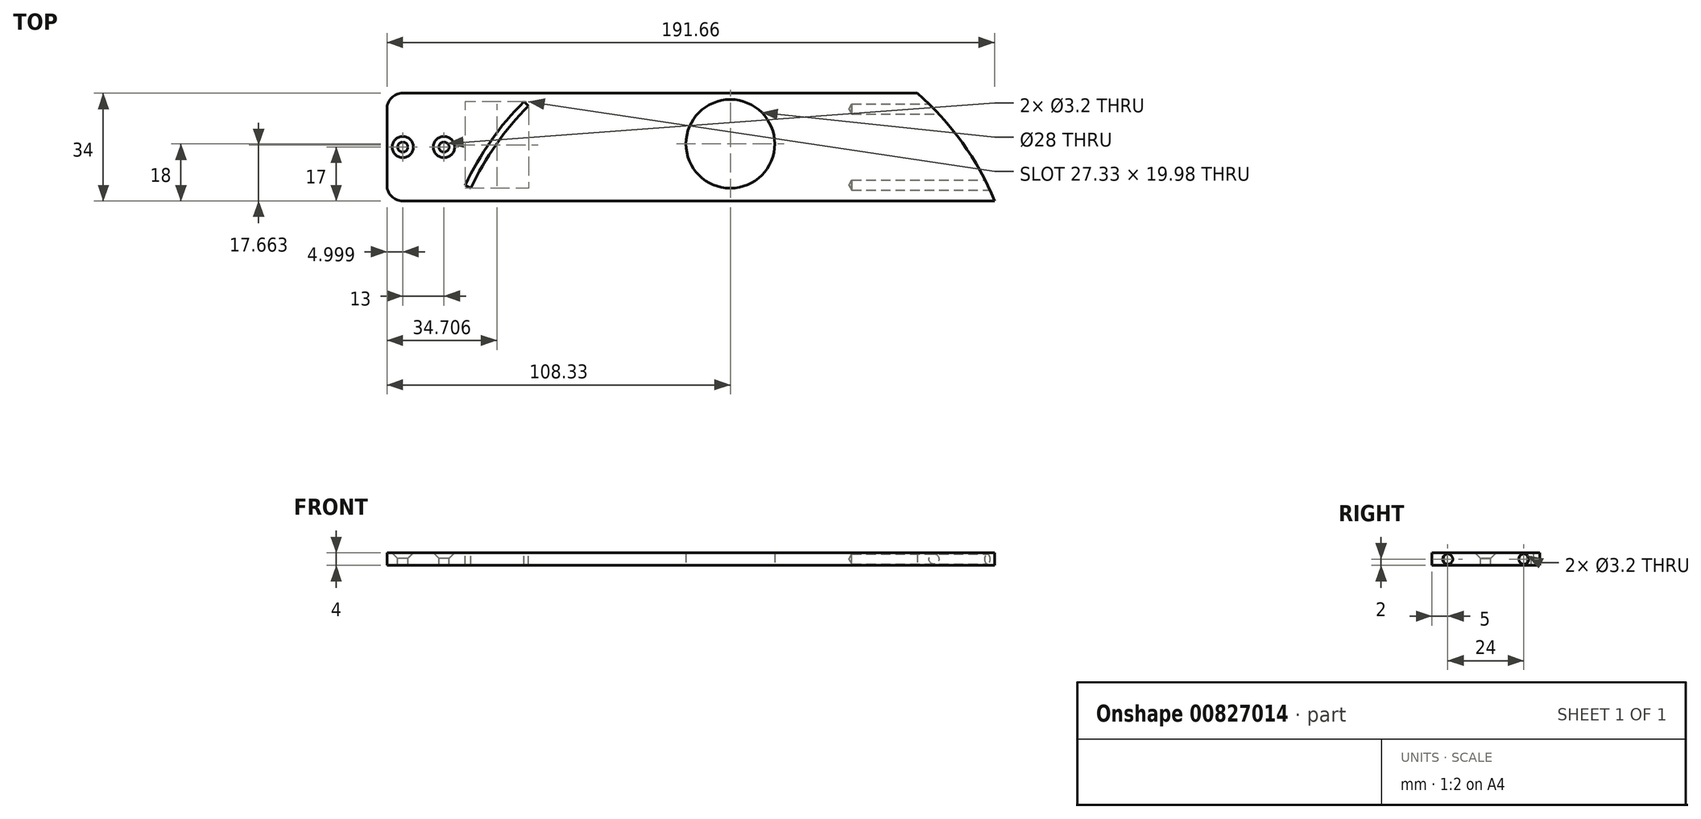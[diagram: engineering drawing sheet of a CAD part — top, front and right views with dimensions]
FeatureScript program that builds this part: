
annotation { "Feature Type Name" : "Feature", "Feature Type Description" : "" }
export const myFeature = defineFeature(function(context is Context, id is Id, definition is map)
    precondition{}
    {
        {
            var Q0;
            Q0=qCreatedBy(makeId("Top.planeOp"),FACE);
            var sketch = newSketch(context, id + "F0", { "sketchPlane" : qUnion([Q0])});
            skCircle(sketch, "E0", {"center": v(0, 0) * mm, "radius": 90 * mm, "construction": true});
            skLineSegment(sketch, "E1", {"start": v(-73.46, 52) * mm, "end": v(73.46, 52) * mm, "construction": true});
            skLineSegment(sketch, "E2", {"start": v(0, 0) * mm, "end": v(0, 90) * mm, "construction": true});
            skCircle(sketch, "E3", {"center": v(0, 52) * mm, "radius": 14 * mm, "construction": true});
            skLineSegment(sketch, "E4.0", {"start": v(-58.96, 68) * mm, "end": v(58.96, 68) * mm, "construction": true});
            skLineSegment(sketch, "E5.MirrorCS", {"start": v(-73.46, 84) * mm, "end": v(73.46, 84) * mm, "construction": true});
            skLineSegment(sketch, "E6.0", {"start": v(-83.33, 34) * mm, "end": v(83.33, 34) * mm, "construction": true});
            skArc(sketch, "E7", {"start": v(83.33, 34) * mm, "mid": v(73.15, 52.44) * mm, "end": v(58.96, 68) * mm});
            skLineSegment(sketch, "E8", {"start": v(-58.96, 68) * mm, "end": v(58.96, 68) * mm});
            skLineSegment(sketch, "E9", {"start": v(-58.96, 68) * mm, "end": v(-108.33, 68) * mm});
            skLineSegment(sketch, "E10", {"start": v(-83.33, 34) * mm, "end": v(-108.33, 34) * mm});
            skLineSegment(sketch, "E11", {"start": v(83.33, 34) * mm, "end": v(-83.33, 34) * mm});
            skLineSegment(sketch, "E12", {"start": v(-108.33, 34) * mm, "end": v(-108.33, 68) * mm});
            skCircle(sketch, "E13", {"center": v(0, 52) * mm, "radius": 57.5 * mm, "construction": true});
            skSolve(sketch);
        }
        {
            var Q0;
            Q0=qCreatedBy(makeId("Right.planeOp"),FACE);
            cPlane(context, id + "F1", {"entities" : qUnion([Q0]), "cplaneType" : CPlaneType.OFFSET, "offset" : 87.27 * mm, "width" : 150 * mm, "height" : 150 * mm});
        }
        {
            var Q0;
            Q0=qCreatedBy(id+"F1.planeOp",FACE);
            var sketch = newSketch(context, id + "F2", { "sketchPlane" : qUnion([Q0])});
            skSolve(sketch);
        }
        {
            var Q0;
            Q0=makeQuery(id+"F0.imprint","IMPRINT",FACE,{"disambiguationData":[TD([[makeQuery(id+"F0.imprint","IMPRINT",EDGE,{"derivedFrom":sQuery(id+"F0.wireOp",EDGE,"E7")}),1.0]])]});
            var Q1;
            Q1 = qSketchRegion(id + "F2", true);
            extrude(context, id + "F3", {"entities" : qUnion([Q0, Q1]), "depth" : 4 * mm, "offsetDistance" : 25 * mm});
        }
        {
            var Q0;
            Q0=makeQuery(id+"F0.imprint","IMPRINT",FACE,{"disambiguationData":[TD([[makeQuery(id+"F0.imprint","IMPRINT",EDGE,{"derivedFrom":sQuery(id+"F0.wireOp",EDGE,"E7")}),1.0]])]});
            extrude(context, id + "F4", {"entities" : qUnion([Q0]), "operationType" : NewBodyOperationType.ADD, "depth" : 4 * mm, "offsetDistance" : 25 * mm});
        }
        {
            var Q0;
            Q0=qCreatedBy(makeId("Right.planeOp"),FACE);
            cPlane(context, id + "F5", {"entities" : qUnion([Q0]), "cplaneType" : CPlaneType.OFFSET, "offset" : 83.3 * mm, "width" : 150 * mm, "height" : 150 * mm});
        }
        {
            var Q0;
            Q0=qCreatedBy(id+"F5.planeOp",FACE);
            var sketch = newSketch(context, id + "F6", { "sketchPlane" : qUnion([Q0])});
            skLineSegment(sketch, "E14", {"start": v(34.24, 2) * mm, "end": v(67.83, 2) * mm, "construction": true});
            skPoint(sketch, "E15", {"position": v(63, 2) * mm});
            skPoint(sketch, "E16", {"position": v(39, 2) * mm});
            skSolve(sketch);
        }
        {
            var Q0;
            Q0=sQuery(id+"F6.wireOp",VERTEX,"E15");
            var Q1;
            Q1=sQuery(id+"F6.wireOp",VERTEX,"E16");
            var Q2;
            Q2=makeQuery(id+"F3.opExtrude","SWEPT_BODY",BODY,{"disambiguationData":[OSD([sQuery(id+"F0.wireOp",EDGE,"E7"),sQuery(id+"F0.wireOp",EDGE,"E8"),sQuery(id+"F0.wireOp",EDGE,"E9"),sQuery(id+"F0.wireOp",EDGE,"E10"),sQuery(id+"F0.wireOp",EDGE,"E11"),sQuery(id+"F0.wireOp",EDGE,"E12")])]});
            hole(context, id + "F7", {"style" : HoleStyle.SIMPLE, "endStyle" : HoleEndStyle.BLIND, "holeDiameter" : 3.2 * mm, "majorDiameter" : 5 * mm, "holeDepth" : 45 * mm, "isTappedThrough" : true, "tappedDepth" : 12 * mm, "tapClearance" : 3, "startFromSketch" : true, "locations" : qUnion([Q0, Q1]), "scope" : qUnion([Q2])});
        }
        {
            var Q0;
            Q0=sQuery(id+"F0.wireOp",VERTEX,"E3.center");
            var Q1;
            Q1=makeQuery(id+"F3.opExtrude","SWEPT_BODY",BODY,{"disambiguationData":[OSD([sQuery(id+"F0.wireOp",EDGE,"E7"),sQuery(id+"F0.wireOp",EDGE,"E8"),sQuery(id+"F0.wireOp",EDGE,"E9"),sQuery(id+"F0.wireOp",EDGE,"E10"),sQuery(id+"F0.wireOp",EDGE,"E11"),sQuery(id+"F0.wireOp",EDGE,"E12")])]});
            hole(context, id + "F8", {"style" : HoleStyle.SIMPLE, "endStyle" : HoleEndStyle.THROUGH, "oppositeDirection" : true, "holeDiameter" : 28 * mm, "majorDiameter" : 5 * mm, "isTappedThrough" : true, "tappedDepth" : 12 * mm, "tapClearance" : 3, "startFromSketch" : true, "locations" : qUnion([Q0]), "scope" : qUnion([Q1])});
        }
        {
            var Q0;
            Q0=makeQuery(id+"F3.opExtrude","CAP_FACE",FACE,{"disambiguationData":[OSD([sQuery(id+"F0.wireOp",EDGE,"E7"),sQuery(id+"F0.wireOp",EDGE,"E8"),sQuery(id+"F0.wireOp",EDGE,"E9"),sQuery(id+"F0.wireOp",EDGE,"E10"),sQuery(id+"F0.wireOp",EDGE,"E11"),sQuery(id+"F0.wireOp",EDGE,"E12")])],"isStart":false});
            var sketch = newSketch(context, id + "F9", { "sketchPlane" : qUnion([Q0])});
            skLineSegment(sketch, "E17", {"start": v(-83.33, 34) * mm, "end": v(-83.33, 68) * mm, "construction": true});
            skLineSegment(sketch, "E18", {"start": v(-108.33, 51) * mm, "end": v(-83.33, 51) * mm, "construction": true});
            skPoint(sketch, "E19", {"position": v(-90.33, 51) * mm});
            skPoint(sketch, "E20", {"position": v(-103.33, 51) * mm});
            skSolve(sketch);
        }
        {
            var Q0;
            Q0=sQuery(id+"F9.wireOp",VERTEX,"E20");
            var Q1;
            Q1=sQuery(id+"F9.wireOp",VERTEX,"E19");
            var Q2;
            Q2=makeQuery(id+"F3.opExtrude","SWEPT_BODY",BODY,{"disambiguationData":[OSD([sQuery(id+"F0.wireOp",EDGE,"E7"),sQuery(id+"F0.wireOp",EDGE,"E8"),sQuery(id+"F0.wireOp",EDGE,"E9"),sQuery(id+"F0.wireOp",EDGE,"E10"),sQuery(id+"F0.wireOp",EDGE,"E11"),sQuery(id+"F0.wireOp",EDGE,"E12")])]});
            hole(context, id + "F10", {"style" : HoleStyle.C_SINK, "endStyle" : HoleEndStyle.BLIND, "holeDiameter" : 3.2 * mm, "cSinkDiameter" : 6.72 * mm, "cSinkAngle" : 90 * degree, "majorDiameter" : 5 * mm, "holeDepth" : 60 * mm, "isTappedThrough" : true, "tappedDepth" : 12 * mm, "tapClearance" : 3, "startFromSketch" : true, "locations" : qUnion([Q0, Q1]), "scope" : qUnion([Q2])});
        }
        {
            var Q0;
            Q0=makeQuery(id+"F3.opExtrude","CAP_FACE",FACE,{"disambiguationData":[OSD([sQuery(id+"F0.wireOp",EDGE,"E7"),sQuery(id+"F0.wireOp",EDGE,"E8"),sQuery(id+"F0.wireOp",EDGE,"E9"),sQuery(id+"F0.wireOp",EDGE,"E10"),sQuery(id+"F0.wireOp",EDGE,"E11"),sQuery(id+"F0.wireOp",EDGE,"E12")])],"isStart":false});
            var sketch = newSketch(context, id + "F11", { "sketchPlane" : qUnion([Q0])});
            skArc(sketch, "E21", {"start": v(-63.63, 64) * mm, "mid": v(-73.9, 51.8) * mm, "end": v(-81.86, 38) * mm});
            skArc(sketch, "E22", {"start": v(-65.13, 65.33) * mm, "mid": v(-75.53, 52.95) * mm, "end": v(-83.62, 38.96) * mm});
            skLineSegment(sketch, "E23", {"start": v(-83.62, 38.96) * mm, "end": v(-81.86, 38) * mm});
            skLineSegment(sketch, "E24", {"start": v(-65.13, 65.33) * mm, "end": v(-63.63, 64) * mm});
            skSolve(sketch);
        }
        {
            var Q0;
            Q0=makeQuery(id+"F11.imprint","IMPRINT",FACE,{"disambiguationData":[TD([[makeQuery(id+"F11.imprint","IMPRINT",EDGE,{"derivedFrom":sQuery(id+"F11.wireOp",EDGE,"E21")}),-1.0]])]});
            extrude(context, id + "F12", {"entities" : qUnion([Q0]), "operationType" : NewBodyOperationType.REMOVE, "endBound" : BoundingType.THROUGH_ALL, "oppositeDirection" : true, "depth" : 16 * mm, "offsetDistance" : 25 * mm});
        }
        {
            var Q0;
            Q0=makeQuery(id+"F3.opExtrude","SWEPT_EDGE",EDGE,{"disambiguationData":[OSD([sQuery(id+"F0.wireOp",EDGE,"E10"),sQuery(id+"F0.wireOp",EDGE,"E12")])]});
            var Q1;
            Q1=makeQuery(id+"F3.opExtrude","SWEPT_EDGE",EDGE,{"disambiguationData":[OSD([sQuery(id+"F0.wireOp",EDGE,"E9"),sQuery(id+"F0.wireOp",EDGE,"E12")])]});
            fillet(context, id + "F13", {"entities" : qUnion([Q0, Q1]), "radius" : 5 * mm, "tangentPropagation" : true, "allowEdgeOverflow" : false});
        }
    });
